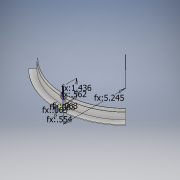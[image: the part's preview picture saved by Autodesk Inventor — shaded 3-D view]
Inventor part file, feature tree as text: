
AUTODESK INVENTOR PART (.ipt)
format: ipt  version: 2017 (Build 210142000, 142)  size: 194,048 bytes
history: native  units: in
note: dims shown in document units (in); Inventor stores cm internally (conversion verified against a paired STEP export)
features: sketch x6, extrude x5, revolve x2, plane x1
ambient origin geometry x8: Origin, YZ Plane, XZ Plane, XY Plane, X Axis, Y Axis, Z Axis, Center Point
bodies: Solid1 (feature_tree)
feature tree (14):
  revolve  "Revolution1"  [1 undecoded]
  plane  "Work Plane1"
  sketch  "Sketch2"  dims[d3=1.4364in d4=0.0625in]
  extrude  "Extrusion2"  Depth=0.0625in
  extrude  "Extrusion3"  TaperAngle=90.0deg  [1 undecoded]
  extrude  "Extrusion4"  Depth=0.375in
  extrude  "Extrusion5"  Depth=1.0in TaperAngle=0.0deg
  revolve  "Revolution2"  [1 undecoded]
  extrude  "Extrusion6"  Depth=0.25in
  sketch  "Sketch1"  dims[d1=0.5536in d2=0.0625in]
  sketch  "Sketch3"  dims[d5=0.0625in d6=90.0deg]
  sketch  "Sketch4"  dims[d7=0.562in d8=0.375in]
  sketch  "Sketch5"  dims[d11=0.3125in d12=1.0in d13=0.0in]
  sketch  "Sketch6"  dims[d14=0.0156in d15=0.0in d16=0.25in d17=0.0625in d18=0.0in d19=135.0deg d20=0.0in d21=0.0in d23=0.0312in d24=0.25in d25=0.25in d27=0.562in d28=90.0deg d29=0.375in d30=1.0in d31=0.0in]
note: 3 required parameter values undecoded (feature->parameter linkage not recoverable at this tier; creation-order binding heuristic only, values carry confidence <= 0.55)